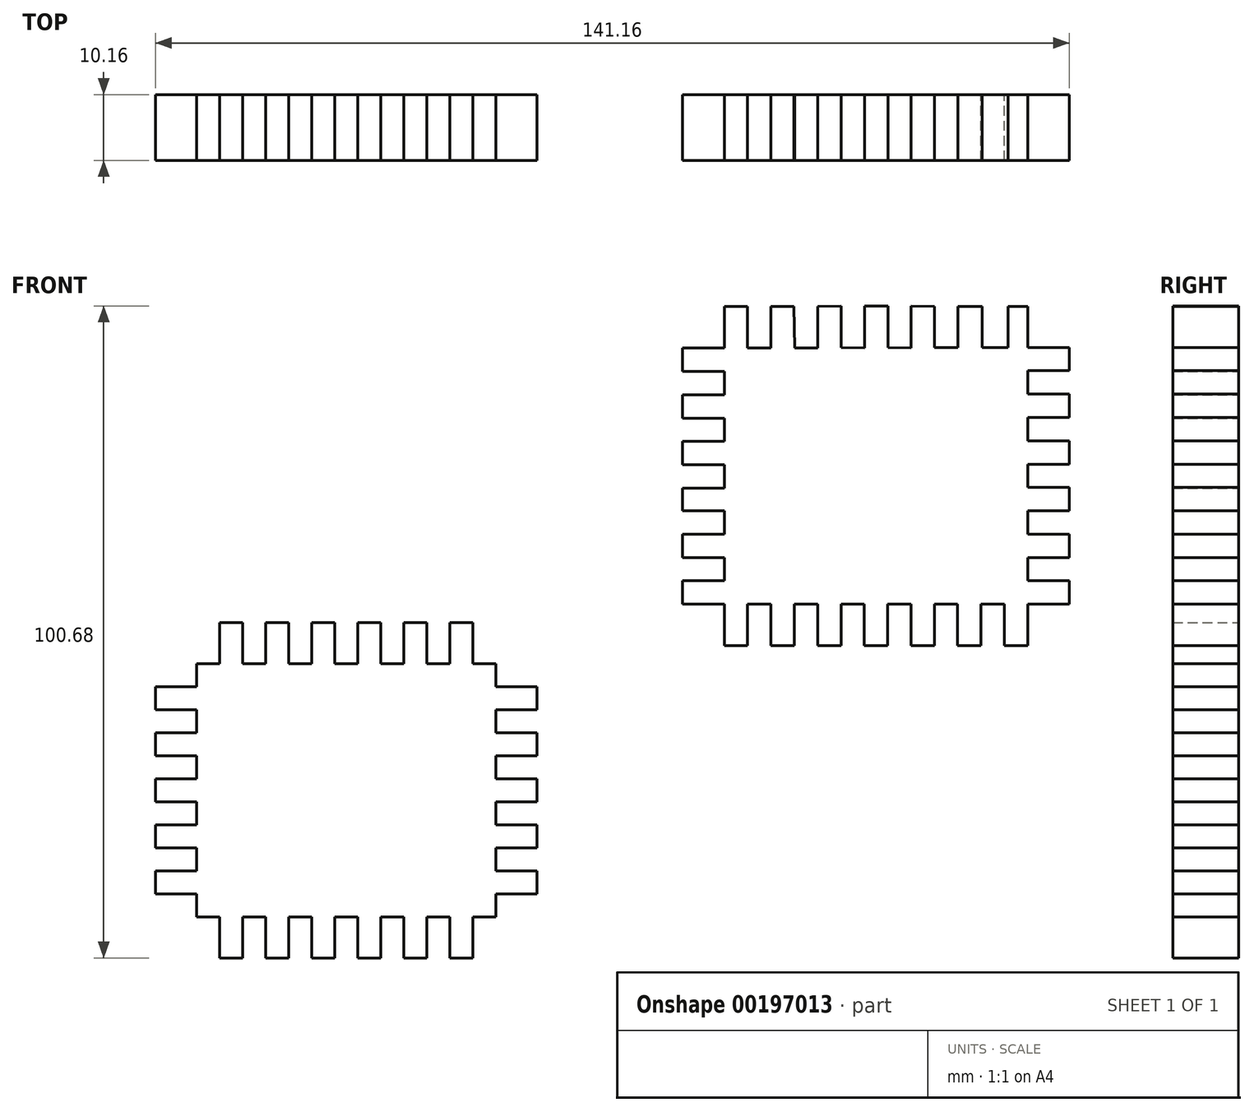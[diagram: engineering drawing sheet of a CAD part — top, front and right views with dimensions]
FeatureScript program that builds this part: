
annotation { "Feature Type Name" : "Feature", "Feature Type Description" : "" }
export const myFeature = defineFeature(function(context is Context, id is Id, definition is map)
    precondition{}
    {
        {
            var Q0;
            Q0=qCreatedBy(makeId("Front.planeOp"),FACE);
            var sketch = newSketch(context, id + "F0", { "sketchPlane" : qUnion([Q0])});
            skPoint(sketch, "E0.middle", {"position": v(0, 0) * mm});
            skLineSegment(sketch, "E1", {"start": v(-10.85, 25.13) * mm, "end": v(-7.25, 25.13) * mm});
            skLineSegment(sketch, "E2", {"start": v(-7.25, 25.13) * mm, "end": v(-7.25, 31.55) * mm});
            skLineSegment(sketch, "E3", {"start": v(-7.25, 31.55) * mm, "end": v(-3.64, 31.6) * mm});
            skLineSegment(sketch, "E4", {"start": v(-3.64, 31.6) * mm, "end": v(-3.64, 25.2) * mm});
            skLineSegment(sketch, "E5", {"start": v(-3.64, 25.2) * mm, "end": v(-0.04, 25.16) * mm});
            skLineSegment(sketch, "E6", {"start": v(-0.04, 25.16) * mm, "end": v(-0.04, 31.62) * mm});
            skLineSegment(sketch, "E7", {"start": v(-0.04, 31.62) * mm, "end": v(3.57, 31.6) * mm});
            skLineSegment(sketch, "E8", {"start": v(3.57, 31.6) * mm, "end": v(3.57, 25.2) * mm});
            skLineSegment(sketch, "E9", {"start": v(3.57, 25.2) * mm, "end": v(7.17, 25.16) * mm});
            skLineSegment(sketch, "E10", {"start": v(7.17, 25.16) * mm, "end": v(7.17, 31.6) * mm});
            skLineSegment(sketch, "E11", {"start": v(7.17, 31.6) * mm, "end": v(10.78, 31.58) * mm});
            skLineSegment(sketch, "E12", {"start": v(10.78, 31.58) * mm, "end": v(10.78, 25.23) * mm});
            skLineSegment(sketch, "E13", {"start": v(10.78, 25.23) * mm, "end": v(14.38, 25.23) * mm});
            skLineSegment(sketch, "E14", {"start": v(14.38, 25.23) * mm, "end": v(14.38, 31.58) * mm});
            skLineSegment(sketch, "E15", {"start": v(14.38, 31.58) * mm, "end": v(18.15, 31.58) * mm});
            skLineSegment(sketch, "E16", {"start": v(18.15, 31.58) * mm, "end": v(18.15, 25.23) * mm});
            skLineSegment(sketch, "E17", {"start": v(18.15, 25.23) * mm, "end": v(22.14, 25.23) * mm});
            skLineSegment(sketch, "E18", {"start": v(22.14, 25.23) * mm, "end": v(22.14, 31.58) * mm});
            skLineSegment(sketch, "E19", {"start": v(22.14, 31.58) * mm, "end": v(25.16, 31.58) * mm});
            skLineSegment(sketch, "E20", {"start": v(-10.85, 25.13) * mm, "end": v(-10.94, 31.58) * mm});
            skPoint(sketch, "E20.endSnap0", {"position": v(-5.44, 31.58) * mm});
            skLineSegment(sketch, "E21", {"start": v(-10.94, 31.58) * mm, "end": v(-14.5, 31.58) * mm});
            skLineSegment(sketch, "E22", {"start": v(-14.5, 31.58) * mm, "end": v(-14.5, 25.13) * mm});
            skLineSegment(sketch, "E23", {"start": v(-14.5, 25.13) * mm, "end": v(-18.1, 25.13) * mm});
            skLineSegment(sketch, "E24", {"start": v(-18.1, 25.13) * mm, "end": v(-18.1, 31.55) * mm});
            skLineSegment(sketch, "E25", {"start": v(-18.1, 31.55) * mm, "end": v(-21.7, 31.55) * mm});
            skLineSegment(sketch, "E26", {"start": v(-21.7, 31.55) * mm, "end": v(-21.7, 25.13) * mm});
            skLineSegment(sketch, "E27", {"start": v(-21.7, 25.13) * mm, "end": v(-28.14, 25.13) * mm});
            skLineSegment(sketch, "E28", {"start": v(-28.14, 25.13) * mm, "end": v(-28.14, 21.52) * mm});
            skLineSegment(sketch, "E29", {"start": v(-28.14, 21.52) * mm, "end": v(-21.7, 21.52) * mm});
            skLineSegment(sketch, "E30", {"start": v(-21.7, 21.52) * mm, "end": v(-21.7, 17.92) * mm});
            skLineSegment(sketch, "E31", {"start": v(-21.7, 17.92) * mm, "end": v(-28.14, 17.92) * mm});
            skLineSegment(sketch, "E32", {"start": v(-28.14, 17.92) * mm, "end": v(-28.14, 14.31) * mm});
            skLineSegment(sketch, "E33", {"start": v(-28.14, 14.31) * mm, "end": v(-21.7, 14.31) * mm});
            skLineSegment(sketch, "E34", {"start": v(-21.7, 14.31) * mm, "end": v(-21.7, 10.71) * mm});
            skLineSegment(sketch, "E35", {"start": v(-21.7, 10.71) * mm, "end": v(-28.14, 10.71) * mm});
            skLineSegment(sketch, "E36", {"start": v(-28.14, 10.71) * mm, "end": v(-28.14, 7.1) * mm});
            skLineSegment(sketch, "E37", {"start": v(-28.14, 7.1) * mm, "end": v(-21.7, 7.1) * mm});
            skLineSegment(sketch, "E38", {"start": v(-21.7, 7.1) * mm, "end": v(-21.7, 3.5) * mm});
            skLineSegment(sketch, "E39", {"start": v(-21.7, 3.5) * mm, "end": v(-28.14, 3.5) * mm});
            skLineSegment(sketch, "E40", {"start": v(-28.14, 3.5) * mm, "end": v(-28.14, -0.1) * mm});
            skLineSegment(sketch, "E41", {"start": v(-28.14, 0) * mm, "end": v(-21.7, 0) * mm});
            skLineSegment(sketch, "E42", {"start": v(-21.7, 0) * mm, "end": v(-21.7, -3.6) * mm});
            skLineSegment(sketch, "E43", {"start": v(-21.7, -3.6) * mm, "end": v(-28.14, -3.6) * mm});
            skLineSegment(sketch, "E44", {"start": v(-28.14, -3.6) * mm, "end": v(-28.14, -7.2) * mm});
            skLineSegment(sketch, "E45", {"start": v(-28.14, -7.2) * mm, "end": v(-21.7, -7.2) * mm});
            skLineSegment(sketch, "E46", {"start": v(-21.7, -7.2) * mm, "end": v(-21.7, -10.81) * mm});
            skLineSegment(sketch, "E47", {"start": v(-21.7, -10.81) * mm, "end": v(-28.14, -10.81) * mm});
            skLineSegment(sketch, "E48", {"start": v(-28.14, -10.81) * mm, "end": v(-28.14, -14.42) * mm});
            skLineSegment(sketch, "E49", {"start": v(-28.14, -14.42) * mm, "end": v(-21.7, -14.42) * mm});
            skLineSegment(sketch, "E50", {"start": v(-21.7, -14.42) * mm, "end": v(-21.7, -20.85) * mm});
            skLineSegment(sketch, "E51", {"start": v(25.16, -20.85) * mm, "end": v(25.16, -14.42) * mm});
            skLineSegment(sketch, "E52", {"start": v(-21.7, -20.85) * mm, "end": v(-18.1, -20.85) * mm});
            skLineSegment(sketch, "E53", {"start": v(-18.1, -20.85) * mm, "end": v(-18.1, -14.42) * mm});
            skLineSegment(sketch, "E54", {"start": v(-18.1, -14.42) * mm, "end": v(-14.5, -14.42) * mm});
            skLineSegment(sketch, "E55", {"start": v(-14.5, -14.42) * mm, "end": v(-14.5, -20.85) * mm});
            skLineSegment(sketch, "E56", {"start": v(-14.5, -20.85) * mm, "end": v(-10.89, -20.85) * mm});
            skLineSegment(sketch, "E57", {"start": v(-10.89, -20.85) * mm, "end": v(-10.89, -14.42) * mm});
            skLineSegment(sketch, "E58", {"start": v(-10.89, -14.42) * mm, "end": v(-7.28, -14.42) * mm});
            skLineSegment(sketch, "E59", {"start": v(-7.28, -14.42) * mm, "end": v(-7.28, -20.85) * mm});
            skLineSegment(sketch, "E60", {"start": v(-7.28, -20.85) * mm, "end": v(-3.68, -20.85) * mm});
            skLineSegment(sketch, "E61", {"start": v(-3.68, -20.85) * mm, "end": v(-3.68, -14.42) * mm});
            skLineSegment(sketch, "E62", {"start": v(-3.68, -14.42) * mm, "end": v(-0.07, -14.42) * mm});
            skLineSegment(sketch, "E63", {"start": v(-0.07, -14.42) * mm, "end": v(-0.07, -20.85) * mm});
            skLineSegment(sketch, "E64", {"start": v(-0.07, -20.85) * mm, "end": v(3.53, -20.85) * mm});
            skLineSegment(sketch, "E65", {"start": v(3.53, -20.85) * mm, "end": v(3.53, -14.42) * mm});
            skLineSegment(sketch, "E66", {"start": v(3.53, -14.42) * mm, "end": v(7.14, -14.42) * mm});
            skLineSegment(sketch, "E67", {"start": v(7.14, -14.42) * mm, "end": v(7.14, -20.85) * mm});
            skLineSegment(sketch, "E68", {"start": v(7.14, -20.85) * mm, "end": v(10.74, -20.85) * mm});
            skLineSegment(sketch, "E69", {"start": v(10.74, -20.85) * mm, "end": v(10.74, -14.42) * mm});
            skLineSegment(sketch, "E70", {"start": v(10.74, -14.42) * mm, "end": v(14.34, -14.42) * mm});
            skLineSegment(sketch, "E71", {"start": v(14.34, -14.42) * mm, "end": v(14.34, -20.85) * mm});
            skLineSegment(sketch, "E72", {"start": v(14.34, -20.85) * mm, "end": v(17.95, -20.85) * mm});
            skLineSegment(sketch, "E73", {"start": v(17.95, -20.85) * mm, "end": v(17.95, -14.42) * mm});
            skLineSegment(sketch, "E74", {"start": v(17.95, -14.42) * mm, "end": v(21.55, -14.42) * mm});
            skLineSegment(sketch, "E75", {"start": v(21.55, -14.42) * mm, "end": v(21.55, -20.85) * mm});
            skLineSegment(sketch, "E76", {"start": v(21.55, -20.85) * mm, "end": v(25.16, -20.85) * mm});
            skLineSegment(sketch, "E77", {"start": v(25.16, 18.02) * mm, "end": v(31.6, 18.02) * mm});
            skLineSegment(sketch, "E78", {"start": v(31.6, 18.02) * mm, "end": v(31.6, 14.42) * mm});
            skLineSegment(sketch, "E79", {"start": v(31.6, 14.42) * mm, "end": v(25.16, 14.42) * mm});
            skLineSegment(sketch, "E80", {"start": v(25.16, 14.42) * mm, "end": v(25.16, 10.81) * mm});
            skLineSegment(sketch, "E81", {"start": v(25.16, 10.81) * mm, "end": v(31.6, 10.81) * mm});
            skLineSegment(sketch, "E82", {"start": v(31.6, 10.81) * mm, "end": v(31.6, 7.2) * mm});
            skLineSegment(sketch, "E83", {"start": v(31.6, 7.2) * mm, "end": v(25.16, 7.2) * mm});
            skLineSegment(sketch, "E84", {"start": v(25.16, 7.2) * mm, "end": v(25.16, 3.6) * mm});
            skLineSegment(sketch, "E85", {"start": v(25.16, 3.6) * mm, "end": v(31.6, 3.6) * mm});
            skLineSegment(sketch, "E86", {"start": v(31.6, 3.6) * mm, "end": v(31.6, 0) * mm});
            skLineSegment(sketch, "E87", {"start": v(25.16, 0) * mm, "end": v(25.16, -3.6) * mm});
            skLineSegment(sketch, "E88", {"start": v(25.16, -3.6) * mm, "end": v(31.6, -3.6) * mm});
            skLineSegment(sketch, "E89", {"start": v(31.6, -3.6) * mm, "end": v(31.6, -7.2) * mm});
            skLineSegment(sketch, "E90", {"start": v(31.6, -7.2) * mm, "end": v(25.16, -7.2) * mm});
            skLineSegment(sketch, "E91", {"start": v(25.16, -7.2) * mm, "end": v(25.16, -10.81) * mm});
            skLineSegment(sketch, "E92", {"start": v(25.16, -10.81) * mm, "end": v(31.6, -10.81) * mm});
            skLineSegment(sketch, "E93", {"start": v(31.6, -10.81) * mm, "end": v(31.6, -14.42) * mm});
            skLineSegment(sketch, "E94", {"start": v(31.6, -14.42) * mm, "end": v(25.16, -14.42) * mm});
            skLineSegment(sketch, "E95", {"start": v(25.16, 18.02) * mm, "end": v(25.16, 21.63) * mm});
            skLineSegment(sketch, "E96", {"start": v(25.16, 21.63) * mm, "end": v(31.6, 21.63) * mm});
            skLineSegment(sketch, "E97", {"start": v(31.6, 21.63) * mm, "end": v(31.6, 25.23) * mm});
            skLineSegment(sketch, "E98", {"start": v(31.6, 25.23) * mm, "end": v(25.16, 25.23) * mm});
            skLineSegment(sketch, "E99", {"start": v(25.16, 25.23) * mm, "end": v(25.16, 31.58) * mm});
            skLineSegment(sketch, "E100", {"start": v(25.16, 0) * mm, "end": v(31.6, 0) * mm});
            skSolve(sketch);
        }
        {
            var Q0;
            Q0=makeQuery(id+"F0.imprint","IMPRINT",FACE,{"disambiguationData":[TD([[makeQuery(id+"F0.imprint","IMPRINT",EDGE,{"derivedFrom":sQuery(id+"F0.wireOp",EDGE,"E1")}),-1.0]])]});
            extrude(context, id + "F1", {"entities" : qUnion([Q0]), "depth" : 10.16 * mm});
        }
        {
            var Q0;
            Q0=qCreatedBy(makeId("Front.planeOp"),FACE);
            var sketch = newSketch(context, id + "F2", { "sketchPlane" : qUnion([Q0])});
            skLineSegment(sketch, "E101", {"start": v(-99.67, -62.7) * mm, "end": v(-99.67, -69.06) * mm});
            skLineSegment(sketch, "E102", {"start": v(-99.67, -69.06) * mm, "end": v(-96.11, -69.06) * mm});
            skLineSegment(sketch, "E103", {"start": v(-96.11, -69.06) * mm, "end": v(-96.11, -62.7) * mm});
            skLineSegment(sketch, "E104", {"start": v(-96.11, -62.7) * mm, "end": v(-92.56, -62.7) * mm});
            skLineSegment(sketch, "E105", {"start": v(-92.56, -62.7) * mm, "end": v(-92.56, -69.06) * mm});
            skLineSegment(sketch, "E106", {"start": v(-92.56, -69.06) * mm, "end": v(-89, -69.06) * mm});
            skLineSegment(sketch, "E107", {"start": v(-89, -69.06) * mm, "end": v(-89, -62.7) * mm});
            skLineSegment(sketch, "E108", {"start": v(-89, -62.7) * mm, "end": v(-85.44, -62.7) * mm});
            skLineSegment(sketch, "E109", {"start": v(-85.44, -62.7) * mm, "end": v(-85.44, -69.06) * mm});
            skLineSegment(sketch, "E110", {"start": v(-85.44, -69.06) * mm, "end": v(-81.89, -69.06) * mm});
            skLineSegment(sketch, "E111", {"start": v(-81.89, -69.06) * mm, "end": v(-81.89, -62.7) * mm});
            skLineSegment(sketch, "E112", {"start": v(-81.89, -62.7) * mm, "end": v(-78.33, -62.7) * mm});
            skLineSegment(sketch, "E113", {"start": v(-78.33, -62.7) * mm, "end": v(-78.33, -69.06) * mm});
            skLineSegment(sketch, "E114", {"start": v(-78.33, -69.06) * mm, "end": v(-74.78, -69.06) * mm});
            skLineSegment(sketch, "E115", {"start": v(-74.78, -69.06) * mm, "end": v(-74.78, -62.7) * mm});
            skLineSegment(sketch, "E116", {"start": v(-74.78, -62.7) * mm, "end": v(-71.22, -62.7) * mm});
            skLineSegment(sketch, "E117", {"start": v(-71.22, -62.7) * mm, "end": v(-71.22, -69.06) * mm});
            skLineSegment(sketch, "E118", {"start": v(-71.22, -69.06) * mm, "end": v(-67.66, -69.06) * mm});
            skLineSegment(sketch, "E119", {"start": v(-67.66, -69.06) * mm, "end": v(-67.66, -62.7) * mm});
            skLineSegment(sketch, "E120", {"start": v(-67.66, -62.7) * mm, "end": v(-64.1, -62.7) * mm});
            skLineSegment(sketch, "E121", {"start": v(-64.1, -62.7) * mm, "end": v(-64.1, -69.06) * mm});
            skLineSegment(sketch, "E122", {"start": v(-64.1, -69.06) * mm, "end": v(-60.55, -69.06) * mm});
            skLineSegment(sketch, "E123", {"start": v(-60.55, -69.06) * mm, "end": v(-60.55, -62.7) * mm});
            skLineSegment(sketch, "E124", {"start": v(-60.55, -62.7) * mm, "end": v(-57, -62.7) * mm});
            skLineSegment(sketch, "E125", {"start": v(-57, -62.7) * mm, "end": v(-57, -59.15) * mm});
            skLineSegment(sketch, "E126", {"start": v(-57, -59.15) * mm, "end": v(-50.65, -59.15) * mm});
            skLineSegment(sketch, "E127", {"start": v(-50.65, -59.15) * mm, "end": v(-50.65, -55.6) * mm});
            skLineSegment(sketch, "E128", {"start": v(-50.65, -55.6) * mm, "end": v(-57, -55.6) * mm});
            skLineSegment(sketch, "E129", {"start": v(-57, -55.6) * mm, "end": v(-57, -52.04) * mm});
            skLineSegment(sketch, "E130", {"start": v(-57, -52.04) * mm, "end": v(-50.65, -52.04) * mm});
            skLineSegment(sketch, "E131", {"start": v(-50.65, -52.04) * mm, "end": v(-50.65, -48.48) * mm});
            skLineSegment(sketch, "E132", {"start": v(-50.65, -48.48) * mm, "end": v(-57, -48.48) * mm});
            skLineSegment(sketch, "E133", {"start": v(-57, -48.48) * mm, "end": v(-57, -44.93) * mm});
            skLineSegment(sketch, "E134", {"start": v(-57, -44.93) * mm, "end": v(-50.65, -44.93) * mm});
            skLineSegment(sketch, "E135", {"start": v(-50.65, -44.93) * mm, "end": v(-50.65, -41.37) * mm});
            skLineSegment(sketch, "E136", {"start": v(-50.65, -41.37) * mm, "end": v(-57, -41.37) * mm});
            skLineSegment(sketch, "E137", {"start": v(-57, -41.37) * mm, "end": v(-57, -37.81) * mm});
            skLineSegment(sketch, "E138", {"start": v(-57, -37.81) * mm, "end": v(-50.65, -37.81) * mm});
            skLineSegment(sketch, "E139", {"start": v(-50.65, -37.81) * mm, "end": v(-50.65, -34.26) * mm});
            skLineSegment(sketch, "E140", {"start": v(-50.65, -34.26) * mm, "end": v(-57, -34.26) * mm});
            skLineSegment(sketch, "E141", {"start": v(-57, -34.26) * mm, "end": v(-57, -30.7) * mm});
            skLineSegment(sketch, "E142", {"start": v(-57, -30.7) * mm, "end": v(-50.65, -30.7) * mm});
            skLineSegment(sketch, "E143", {"start": v(-50.65, -30.7) * mm, "end": v(-50.65, -27.15) * mm});
            skLineSegment(sketch, "E144", {"start": v(-50.65, -27.15) * mm, "end": v(-57, -27.15) * mm});
            skLineSegment(sketch, "E145", {"start": v(-57, -27.15) * mm, "end": v(-57, -23.59) * mm});
            skLineSegment(sketch, "E146", {"start": v(-57, -23.59) * mm, "end": v(-60.55, -23.59) * mm});
            skLineSegment(sketch, "E147", {"start": v(-99.67, -23.59) * mm, "end": v(-99.67, -17.24) * mm});
            skLineSegment(sketch, "E148", {"start": v(-60.55, -17.24) * mm, "end": v(-60.55, -23.59) * mm});
            skLineSegment(sketch, "E149", {"start": v(-60.55, -17.24) * mm, "end": v(-64.1, -17.24) * mm});
            skLineSegment(sketch, "E150", {"start": v(-64.1, -17.24) * mm, "end": v(-64.1, -23.59) * mm});
            skLineSegment(sketch, "E151", {"start": v(-64.1, -23.59) * mm, "end": v(-67.66, -23.59) * mm});
            skLineSegment(sketch, "E152", {"start": v(-67.66, -23.59) * mm, "end": v(-67.66, -17.24) * mm});
            skLineSegment(sketch, "E153", {"start": v(-71.22, -17.24) * mm, "end": v(-71.22, -23.59) * mm});
            skLineSegment(sketch, "E154", {"start": v(-71.22, -23.59) * mm, "end": v(-74.78, -23.59) * mm});
            skLineSegment(sketch, "E155", {"start": v(-74.78, -23.59) * mm, "end": v(-74.78, -17.24) * mm});
            skLineSegment(sketch, "E156", {"start": v(-74.78, -17.24) * mm, "end": v(-78.33, -17.24) * mm});
            skLineSegment(sketch, "E157", {"start": v(-78.33, -17.24) * mm, "end": v(-78.33, -23.59) * mm});
            skLineSegment(sketch, "E158", {"start": v(-78.33, -23.59) * mm, "end": v(-81.89, -23.59) * mm});
            skLineSegment(sketch, "E159", {"start": v(-81.89, -23.59) * mm, "end": v(-81.89, -17.24) * mm});
            skLineSegment(sketch, "E160", {"start": v(-81.89, -17.24) * mm, "end": v(-85.44, -17.24) * mm});
            skLineSegment(sketch, "E161", {"start": v(-85.44, -17.24) * mm, "end": v(-85.44, -23.59) * mm});
            skLineSegment(sketch, "E162", {"start": v(-85.44, -23.59) * mm, "end": v(-89, -23.59) * mm});
            skLineSegment(sketch, "E163", {"start": v(-89, -23.59) * mm, "end": v(-89, -17.24) * mm});
            skLineSegment(sketch, "E164", {"start": v(-89, -17.24) * mm, "end": v(-92.56, -17.24) * mm});
            skLineSegment(sketch, "E165", {"start": v(-92.56, -17.24) * mm, "end": v(-92.56, -23.59) * mm});
            skLineSegment(sketch, "E166", {"start": v(-92.56, -23.59) * mm, "end": v(-96.11, -23.59) * mm});
            skLineSegment(sketch, "E167", {"start": v(-96.11, -23.59) * mm, "end": v(-96.11, -17.24) * mm});
            skLineSegment(sketch, "E168", {"start": v(-96.11, -17.24) * mm, "end": v(-99.67, -17.24) * mm});
            skLineSegment(sketch, "E169", {"start": v(-99.67, -23.59) * mm, "end": v(-103.22, -23.59) * mm});
            skLineSegment(sketch, "E170", {"start": v(-99.67, -62.7) * mm, "end": v(-103.22, -62.7) * mm});
            skLineSegment(sketch, "E171", {"start": v(-71.22, -17.24) * mm, "end": v(-67.66, -17.24) * mm});
            skLineSegment(sketch, "E172", {"start": v(-103.22, -23.59) * mm, "end": v(-103.22, -27.15) * mm});
            skLineSegment(sketch, "E173", {"start": v(-103.22, -27.15) * mm, "end": v(-109.57, -27.15) * mm});
            skLineSegment(sketch, "E174", {"start": v(-109.57, -27.15) * mm, "end": v(-109.57, -30.7) * mm});
            skLineSegment(sketch, "E175", {"start": v(-109.57, -30.7) * mm, "end": v(-103.22, -30.7) * mm});
            skLineSegment(sketch, "E176", {"start": v(-103.22, -30.7) * mm, "end": v(-103.22, -34.26) * mm});
            skLineSegment(sketch, "E177", {"start": v(-103.22, -34.26) * mm, "end": v(-109.57, -34.26) * mm});
            skLineSegment(sketch, "E178", {"start": v(-109.57, -34.26) * mm, "end": v(-109.57, -37.81) * mm});
            skLineSegment(sketch, "E179", {"start": v(-109.57, -37.81) * mm, "end": v(-103.22, -37.81) * mm});
            skLineSegment(sketch, "E180", {"start": v(-103.22, -37.81) * mm, "end": v(-103.22, -41.37) * mm});
            skLineSegment(sketch, "E181", {"start": v(-103.22, -41.37) * mm, "end": v(-109.57, -41.37) * mm});
            skLineSegment(sketch, "E182", {"start": v(-109.57, -41.37) * mm, "end": v(-109.57, -44.93) * mm});
            skLineSegment(sketch, "E183", {"start": v(-109.57, -44.93) * mm, "end": v(-103.22, -44.93) * mm});
            skLineSegment(sketch, "E184", {"start": v(-103.22, -44.93) * mm, "end": v(-103.22, -48.48) * mm});
            skLineSegment(sketch, "E185", {"start": v(-103.22, -48.48) * mm, "end": v(-109.57, -48.48) * mm});
            skLineSegment(sketch, "E186", {"start": v(-109.57, -48.48) * mm, "end": v(-109.57, -52.04) * mm});
            skLineSegment(sketch, "E187", {"start": v(-109.57, -52.04) * mm, "end": v(-103.22, -52.04) * mm});
            skLineSegment(sketch, "E188", {"start": v(-103.22, -52.04) * mm, "end": v(-103.22, -55.6) * mm});
            skLineSegment(sketch, "E189", {"start": v(-103.22, -55.6) * mm, "end": v(-109.57, -55.6) * mm});
            skLineSegment(sketch, "E190", {"start": v(-109.57, -55.6) * mm, "end": v(-109.57, -59.15) * mm});
            skLineSegment(sketch, "E191", {"start": v(-109.57, -59.15) * mm, "end": v(-103.22, -59.15) * mm});
            skLineSegment(sketch, "E192", {"start": v(-103.22, -59.15) * mm, "end": v(-103.22, -62.7) * mm});
            skSolve(sketch);
        }
        {
            var Q0;
            Q0=makeQuery(id+"F2.imprint","IMPRINT",FACE,{"disambiguationData":[TD([[makeQuery(id+"F2.imprint","IMPRINT",EDGE,{"derivedFrom":sQuery(id+"F2.wireOp",EDGE,"E101")}),1.0]])]});
            extrude(context, id + "F3", {"entities" : qUnion([Q0]), "depth" : 10.16 * mm});
        }
    });
